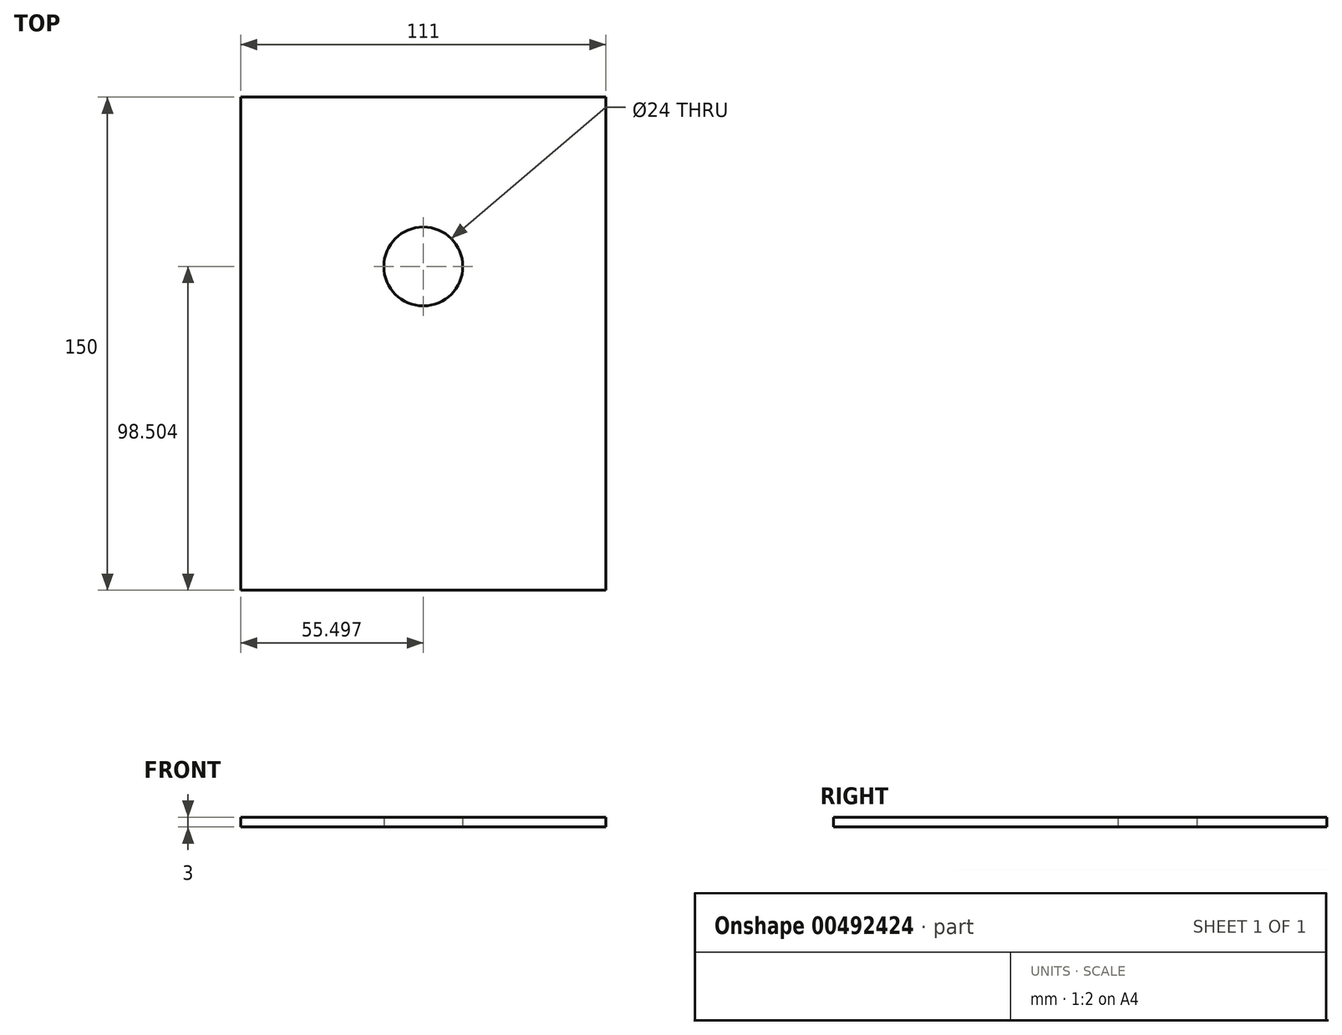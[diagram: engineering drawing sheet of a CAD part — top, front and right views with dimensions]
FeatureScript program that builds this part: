
annotation { "Feature Type Name" : "Feature", "Feature Type Description" : "" }
export const myFeature = defineFeature(function(context is Context, id is Id, definition is map)
    precondition{}
    {
        {
            var Q0;
            Q0=qCreatedBy(makeId("Top.planeOp"),FACE);
            var sketch = newSketch(context, id + "F0", { "sketchPlane" : qUnion([Q0])});
            skLineSegment(sketch, "E0.bottom", {"start": v(-55.7, 40.54) * mm, "end": v(55.3, 40.54) * mm});
            skLineSegment(sketch, "E0.top", {"start": v(-55.7, -109.46) * mm, "end": v(55.3, -109.46) * mm});
            skLineSegment(sketch, "E0.left", {"start": v(-55.7, 40.54) * mm, "end": v(-55.7, -109.46) * mm});
            skLineSegment(sketch, "E0.right", {"start": v(55.3, 40.54) * mm, "end": v(55.3, -109.46) * mm});
            skCircle(sketch, "E1", {"center": v(-0.2, -10.96) * mm, "radius": 12 * mm});
            skSolve(sketch);
        }
        {
            var Q0;
            Q0=makeQuery(id+"F0.imprint","IMPRINT",FACE,{"disambiguationData":[TD([[makeQuery(id+"F0.imprint","IMPRINT",EDGE,{"derivedFrom":sQuery(id+"F0.wireOp",EDGE,"E0.bottom")}),-1.0]])]});
            extrude(context, id + "F1", {"entities" : qUnion([Q0]), "depth" : 3 * mm});
        }
    });
